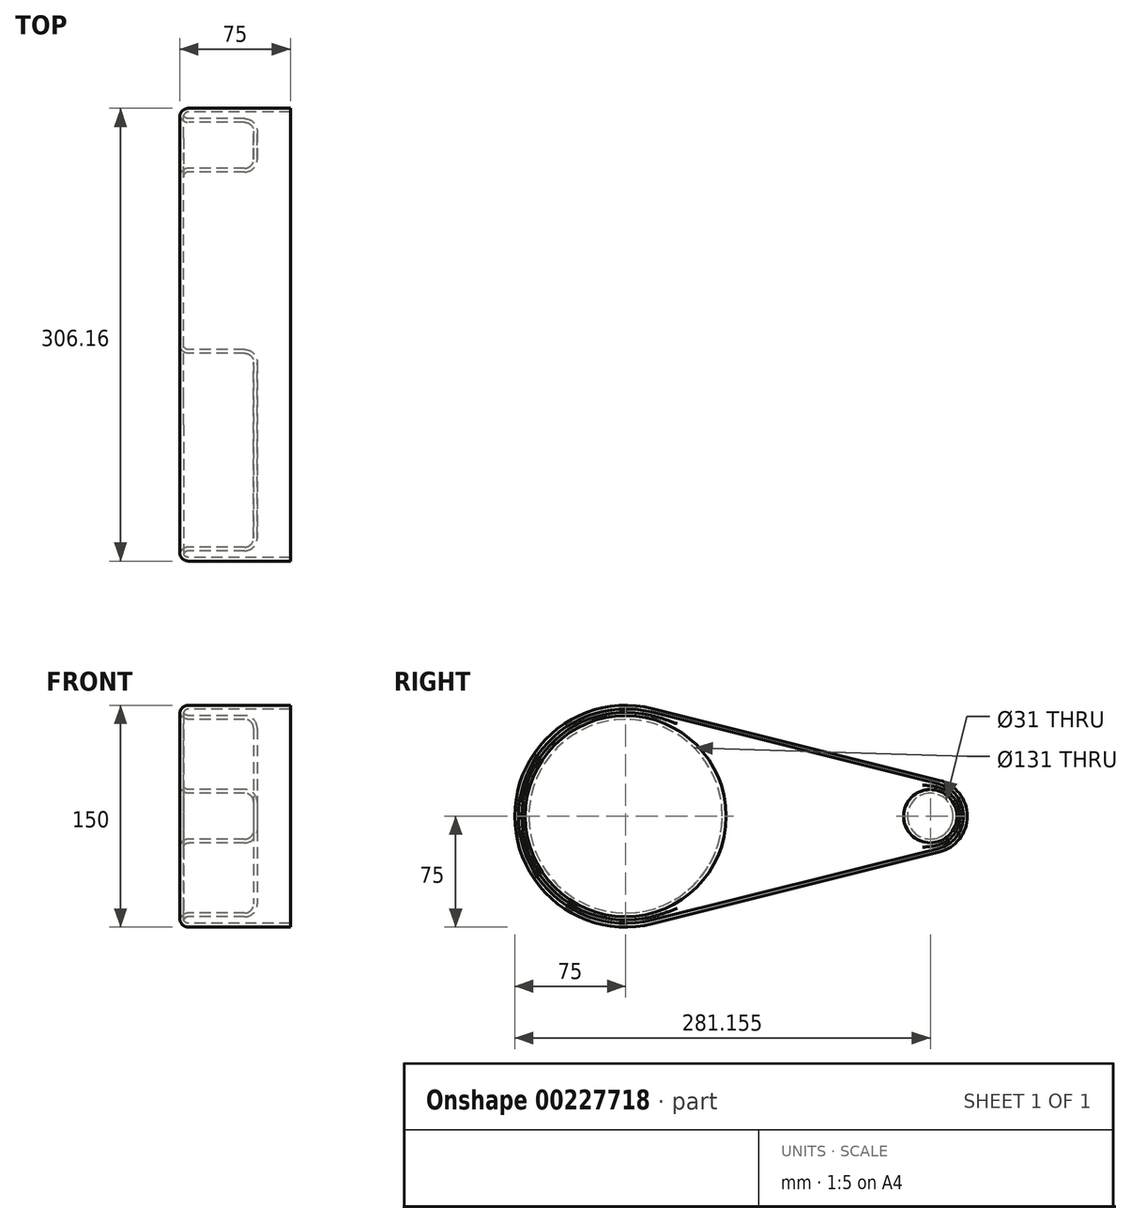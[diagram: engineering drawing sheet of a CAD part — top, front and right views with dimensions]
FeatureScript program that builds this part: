
annotation { "Feature Type Name" : "Feature", "Feature Type Description" : "" }
export const myFeature = defineFeature(function(context is Context, id is Id, definition is map)
    precondition{}
    {
        {
            var Q0;
            Q0=qCreatedBy(makeId("Right.planeOp"),FACE);
            var sketch = newSketch(context, id + "F0", { "sketchPlane" : qUnion([Q0])});
            skCircle(sketch, "E0", {"center": v(0, 0) * mm, "radius": 75 * mm});
            skCircle(sketch, "E1", {"center": v(206.16, 0) * mm, "radius": 25 * mm});
            skLineSegment(sketch, "E2", {"start": v(18.2, 72.76) * mm, "end": v(212.22, 24.25) * mm});
            skLineSegment(sketch, "E3", {"start": v(18.2, -72.76) * mm, "end": v(212.22, -24.25) * mm});
            skSolve(sketch);
        }
        {
            var Q0;
            {var subQ0=sQuery(id+"F0.wireOp",EDGE,"E2");Q0=makeQuery(id+"F0.imprint","IMPRINT",FACE,{"disambiguationData":[TD([[makeQuery(id+"F0.imprint","IMPRINT",EDGE,{"derivedFrom":subQ0}),-1.0]])]});}
            var Q1;
            {var subQ0=sQuery(id+"F0.wireOp",EDGE,"E0");var subQ1=makeQuery(id+"F0.imprint","INTERSECT",VERTEX,{"derivedFrom":[subQ0,sQuery(id+"F0.wireOp",EDGE,"E2")]});Q1=makeQuery(id+"F0.imprint","IMPRINT",FACE,{"disambiguationData":[TD([[makeQuery(id+"F0.imprint","IMPRINT",EDGE,{"disambiguationData":[TD([[subQ1,-1.0]])],"derivedFrom":subQ0}),1.0]])]});}
            var Q2;
            {var subQ0=sQuery(id+"F0.wireOp",EDGE,"E1");var subQ1=makeQuery(id+"F0.imprint","INTERSECT",VERTEX,{"derivedFrom":[subQ0,sQuery(id+"F0.wireOp",EDGE,"E2")]});Q2=makeQuery(id+"F0.imprint","IMPRINT",FACE,{"disambiguationData":[TD([[makeQuery(id+"F0.imprint","IMPRINT",EDGE,{"disambiguationData":[TD([[subQ1,-1.0]])],"derivedFrom":subQ0}),1.0]])]});}
            extrude(context, id + "F1", {"entities" : qUnion([Q0, Q1, Q2]), "depth" : 75 * mm});
        }
        {
            var Q0;
            Q0=makeQuery(id+"F1.opExtrude","CAP_FACE",FACE,{"disambiguationData":[OSD([sQuery(id+"F0.wireOp",EDGE,"E0"),sQuery(id+"F0.wireOp",EDGE,"E1"),sQuery(id+"F0.wireOp",EDGE,"E2"),sQuery(id+"F0.wireOp",EDGE,"E3")])],"isStart":true});
            var sketch = newSketch(context, id + "F2", { "sketchPlane" : qUnion([Q0])});
            skCircle(sketch, "E4", {"center": v(0, 0) * mm, "radius": 65.5 * mm});
            skCircle(sketch, "E5", {"center": v(-206.16, 0) * mm, "radius": 15.5 * mm});
            skSolve(sketch);
        }
        {
            var Q0;
            Q0=makeQuery(id+"F2.imprint","IMPRINT",FACE,{"disambiguationData":[TD([[makeQuery(id+"F2.imprint","IMPRINT",EDGE,{"derivedFrom":sQuery(id+"F2.wireOp",EDGE,"E4")}),1.0]])]});
            var Q1;
            Q1=makeQuery(id+"F2.imprint","IMPRINT",FACE,{"disambiguationData":[TD([[makeQuery(id+"F2.imprint","IMPRINT",EDGE,{"derivedFrom":sQuery(id+"F2.wireOp",EDGE,"E5")}),1.0]])]});
            extrude(context, id + "F3", {"entities" : qUnion([Q0, Q1]), "operationType" : NewBodyOperationType.REMOVE, "oppositeDirection" : true, "depth" : 50 * mm});
        }
        {
            var Q0;
            Q0=makeQuery(id+"F1.opExtrude","CAP_FACE",FACE,{"disambiguationData":[OSD([sQuery(id+"F0.wireOp",EDGE,"E0"),sQuery(id+"F0.wireOp",EDGE,"E1"),sQuery(id+"F0.wireOp",EDGE,"E2"),sQuery(id+"F0.wireOp",EDGE,"E3")])],"isStart":true});
            var Q1;
            Q1=makeQuery(id+"F3.boolean.opBoolean","COPY",FACE,{"derivedFrom":makeQuery(id+"F3.opExtrude","CAP_FACE",FACE,{"disambiguationData":[OSD([sQuery(id+"F2.wireOp",EDGE,"E4")])],"isStart":false})});
            var Q2;
            Q2=makeQuery(id+"F3.boolean.opBoolean","COPY",EDGE,{"derivedFrom":makeQuery(id+"F3.opExtrude","CAP_EDGE",EDGE,{"disambiguationData":[OSD([sQuery(id+"F2.wireOp",EDGE,"E5")])],"isStart":false})});
            fillet(context, id + "F4", {"entities" : qUnion([Q0, Q1, Q2]), "radius" : 6 * mm, "tangentPropagation" : true, "allowEdgeOverflow" : false});
        }
        {
            var Q0;
            Q0=makeQuery(id+"F1.opExtrude","CAP_FACE",FACE,{"disambiguationData":[OSD([sQuery(id+"F0.wireOp",EDGE,"E0"),sQuery(id+"F0.wireOp",EDGE,"E1"),sQuery(id+"F0.wireOp",EDGE,"E2"),sQuery(id+"F0.wireOp",EDGE,"E3")])],"isStart":false});
            shell(context, id + "F5", {"entities" : qUnion([Q0]), "thickness" : 2.5 * mm});
        }
    });
